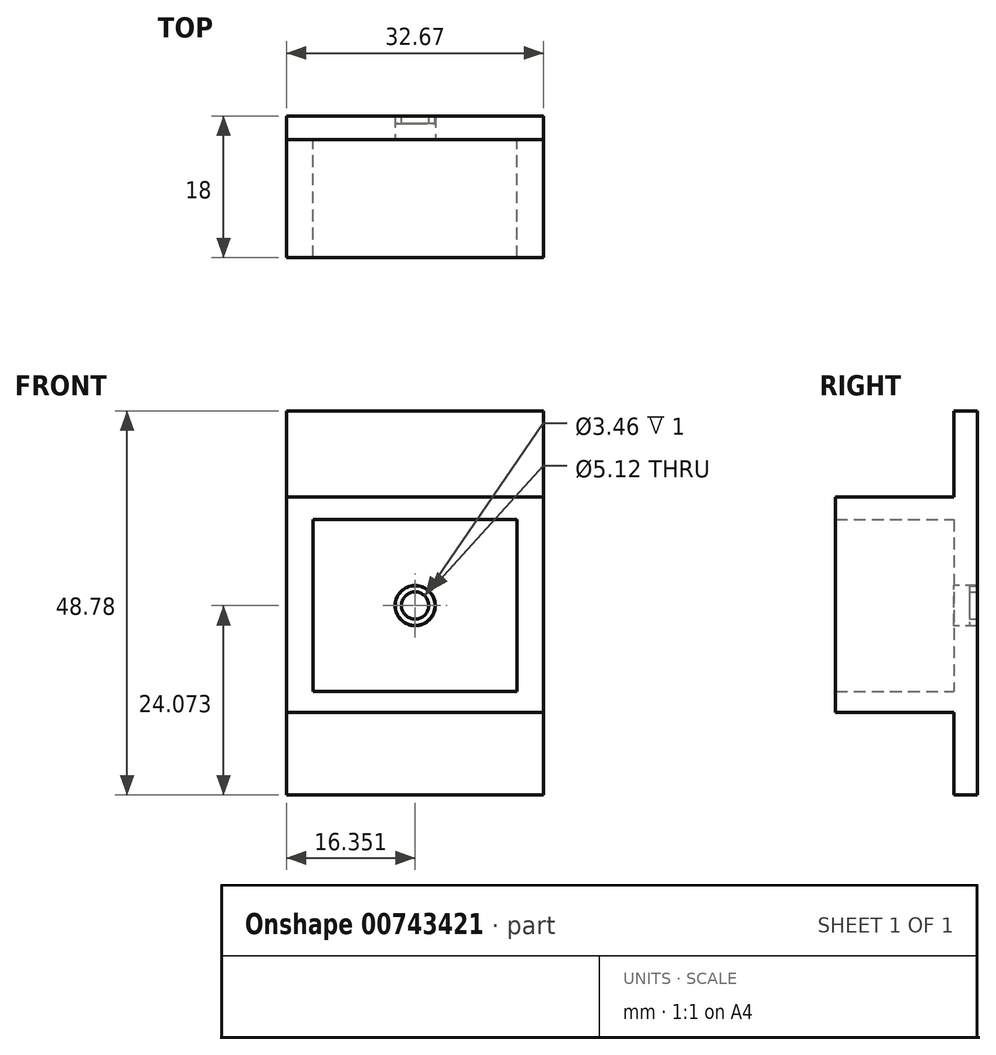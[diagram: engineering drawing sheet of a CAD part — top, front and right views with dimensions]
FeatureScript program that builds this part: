
annotation { "Feature Type Name" : "Feature", "Feature Type Description" : "" }
export const myFeature = defineFeature(function(context is Context, id is Id, definition is map)
    precondition{}
    {
        {
            var Q0;
            Q0=qCreatedBy(makeId("Front.planeOp"),FACE);
            var sketch = newSketch(context, id + "F0", { "sketchPlane" : qUnion([Q0])});
            skLineSegment(sketch, "E0.bottom", {"start": v(0, 0) * mm, "end": v(32.67, 0) * mm});
            skLineSegment(sketch, "E0.top", {"start": v(0, 48.78) * mm, "end": v(32.67, 48.78) * mm});
            skLineSegment(sketch, "E0.left", {"start": v(0, 0) * mm, "end": v(0, 48.78) * mm});
            skLineSegment(sketch, "E0.right", {"start": v(32.67, 0) * mm, "end": v(32.67, 48.78) * mm});
            skSolve(sketch);
        }
        {
            var Q0;
            Q0 = qSketchRegion(id + "F0", true);
            extrude(context, id + "F1", {"entities" : qUnion([Q0]), "depth" : 3 * mm, "offsetDistance" : 25 * mm});
        }
        {
            var Q0;
            Q0=makeQuery(id+"F1.opExtrude","CAP_FACE",FACE,{"disambiguationData":[OSD([sQuery(id+"F0.wireOp",EDGE,"E0.bottom"),sQuery(id+"F0.wireOp",EDGE,"E0.top"),sQuery(id+"F0.wireOp",EDGE,"E0.left"),sQuery(id+"F0.wireOp",EDGE,"E0.right")])],"isStart":false});
            var sketch = newSketch(context, id + "F2", { "sketchPlane" : qUnion([Q0])});
            skLineSegment(sketch, "E1", {"start": v(0, 10.48) * mm, "end": v(32.67, 10.48) * mm});
            skLineSegment(sketch, "E2", {"start": v(32.67, 10.48) * mm, "end": v(32.67, 37.84) * mm});
            skLineSegment(sketch, "E3", {"start": v(32.67, 37.84) * mm, "end": v(0, 37.84) * mm});
            skLineSegment(sketch, "E4", {"start": v(0, 10.48) * mm, "end": v(0, 37.84) * mm});
            skLineSegment(sketch, "E5", {"start": v(16.33, 35) * mm, "end": v(3.4, 35) * mm});
            skLineSegment(sketch, "E6.bottom", {"start": v(3.4, 35) * mm, "end": v(29.3, 35) * mm});
            skLineSegment(sketch, "E6.top", {"start": v(3.4, 13.14) * mm, "end": v(29.3, 13.14) * mm});
            skLineSegment(sketch, "E6.left", {"start": v(3.4, 35) * mm, "end": v(3.4, 13.14) * mm});
            skLineSegment(sketch, "E6.right", {"start": v(29.3, 35) * mm, "end": v(29.3, 13.14) * mm});
            skSolve(sketch);
        }
        {
            var Q0;
            Q0 = qSketchRegion(id + "F2", true);
            extrude(context, id + "F3", {"entities" : qUnion([Q0]), "operationType" : NewBodyOperationType.ADD, "depth" : 15 * mm, "offsetDistance" : 25 * mm});
        }
        {
            var Q0;
            Q0=makeQuery(id+"F3.boolean.opBoolean","SPLIT",FACE,{"disambiguationData":[TD([makeQuery(id+"F3.opExtrude","SWEPT_FACE",FACE,{"disambiguationData":[OSD([sQuery(id+"F2.wireOp",EDGE,"E6.bottom")])]})])],"derivedFrom":makeQuery(id+"F1.opExtrude","CAP_FACE",FACE,{"disambiguationData":[OSD([sQuery(id+"F0.wireOp",EDGE,"E0.bottom"),sQuery(id+"F0.wireOp",EDGE,"E0.top"),sQuery(id+"F0.wireOp",EDGE,"E0.left"),sQuery(id+"F0.wireOp",EDGE,"E0.right")])],"isStart":false})});
            var sketch = newSketch(context, id + "F4", { "sketchPlane" : qUnion([Q0])});
            skCircle(sketch, "E7", {"center": v(16.35, 24.07) * mm, "radius": 2.56 * mm});
            skPoint(sketch, "E7.centerSnap0", {"position": v(3.4, 24.07) * mm});
            skPoint(sketch, "E7.centerSnap1", {"position": v(16.35, 35) * mm});
            skSolve(sketch);
        }
        {
            var Q0;
            Q0 = qSketchRegion(id + "F4", true);
            extrude(context, id + "F5", {"entities" : qUnion([Q0]), "operationType" : NewBodyOperationType.REMOVE, "oppositeDirection" : true, "depth" : 25 * mm, "offsetDistance" : 25 * mm});
        }
        {
            var Q0;
            Q0=makeQuery(id+"F1.opExtrude","CAP_FACE",FACE,{"disambiguationData":[OSD([sQuery(id+"F0.wireOp",EDGE,"E0.bottom"),sQuery(id+"F0.wireOp",EDGE,"E0.top"),sQuery(id+"F0.wireOp",EDGE,"E0.left"),sQuery(id+"F0.wireOp",EDGE,"E0.right")])],"isStart":true});
            var sketch = newSketch(context, id + "F6", { "sketchPlane" : qUnion([Q0])});
            skCircle(sketch, "E8", {"center": v(-16.35, 24.07) * mm, "radius": 2.51 * mm});
            skCircle(sketch, "E9", {"center": v(-16.35, 24.07) * mm, "radius": 1.73 * mm});
            skSolve(sketch);
        }
        {
            var Q0;
            Q0 = qSketchRegion(id + "F6", true);
            extrude(context, id + "F7", {"entities" : qUnion([Q0]), "oppositeDirection" : true, "depth" : 1 * mm, "offsetDistance" : 25 * mm});
        }
    });
